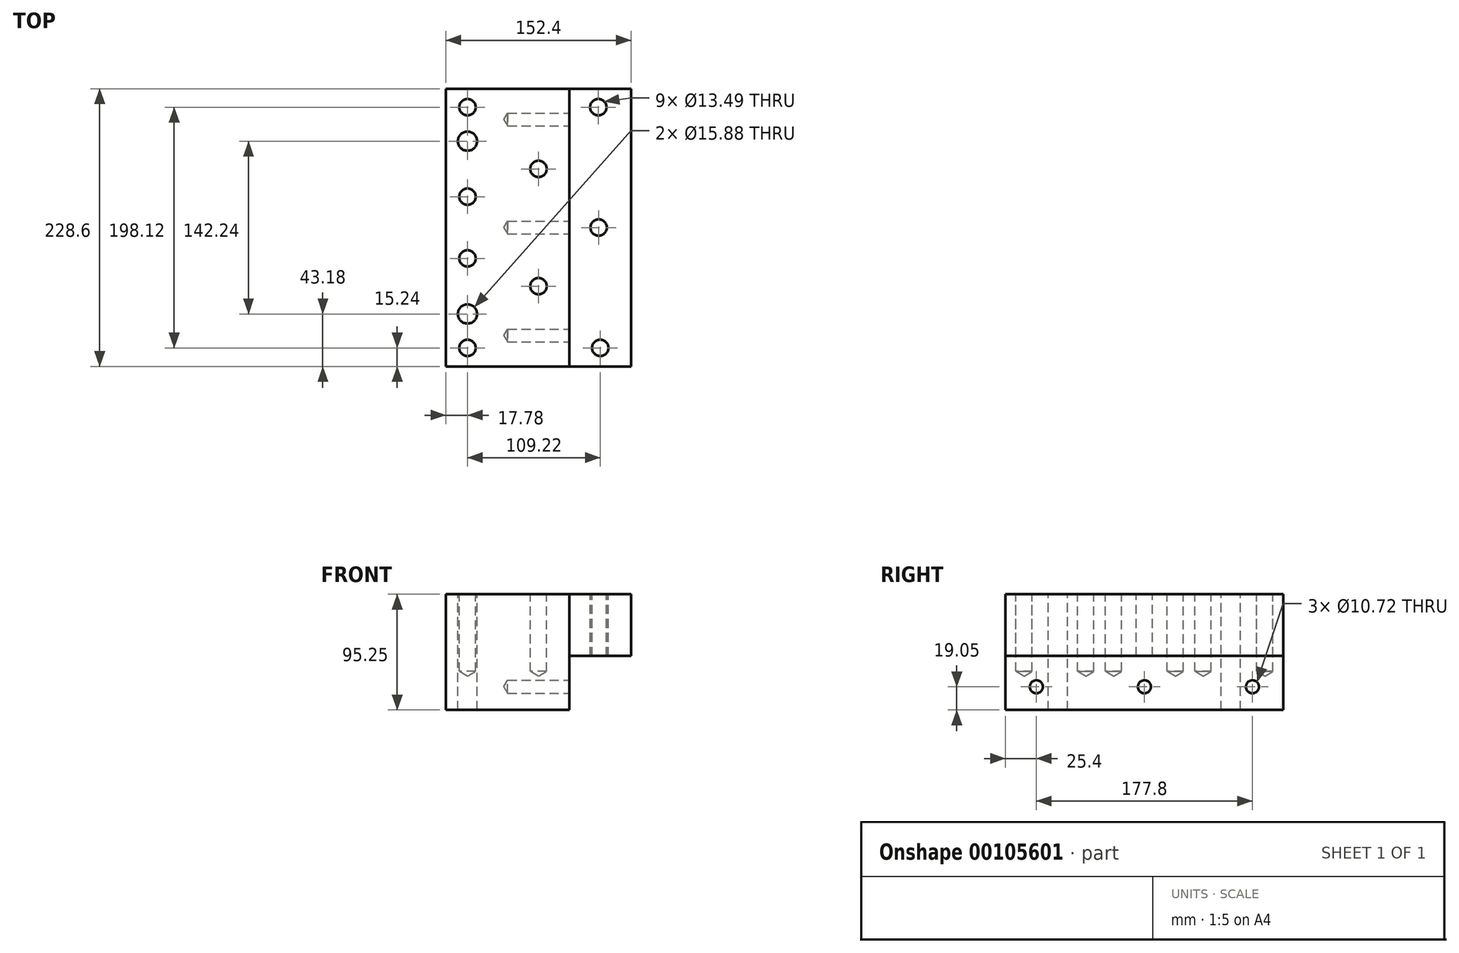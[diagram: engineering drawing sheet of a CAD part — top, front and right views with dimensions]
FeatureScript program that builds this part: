
annotation { "Feature Type Name" : "Feature", "Feature Type Description" : "" }
export const myFeature = defineFeature(function(context is Context, id is Id, definition is map)
    precondition{}
    {
        {
            var Q0;
            Q0=qCreatedBy(makeId("Top.planeOp"),FACE);
            var sketch = newSketch(context, id + "F0", { "sketchPlane" : qUnion([Q0])});
            skLineSegment(sketch, "E0.bottom", {"start": v(-76.2, 114.3) * mm, "end": v(76.2, 114.3) * mm});
            skLineSegment(sketch, "E0.top", {"start": v(-76.2, -114.3) * mm, "end": v(76.2, -114.3) * mm});
            skLineSegment(sketch, "E0.left", {"start": v(-76.2, 114.3) * mm, "end": v(-76.2, -114.3) * mm});
            skLineSegment(sketch, "E0.right", {"start": v(76.2, 114.3) * mm, "end": v(76.2, -114.3) * mm});
            skPoint(sketch, "E0.middle", {"position": v(0, 0) * mm});
            skLineSegment(sketch, "E1", {"start": v(25.4, 114.3) * mm, "end": v(25.4, -114.3) * mm});
            skSolve(sketch);
        }
        {
            var Q0;
            {var subQ0=sQuery(id+"F0.wireOp",EDGE,"E0.left");Q0=makeQuery(id+"F0.imprint","IMPRINT",FACE,{"disambiguationData":[TD([[makeQuery(id+"F0.imprint","IMPRINT",EDGE,{"derivedFrom":subQ0}),1.0]])]});}
            extrude(context, id + "F1", {"entities" : qUnion([Q0]), "oppositeDirection" : true, "depth" : 95.25 * mm});
        }
        {
            var Q0;
            {var subQ0=sQuery(id+"F0.wireOp",EDGE,"E0.right");Q0=makeQuery(id+"F0.imprint","IMPRINT",FACE,{"disambiguationData":[TD([[makeQuery(id+"F0.imprint","IMPRINT",EDGE,{"derivedFrom":subQ0}),-1.0]])]});}
            extrude(context, id + "F2", {"entities" : qUnion([Q0]), "oppositeDirection" : true, "depth" : 50.8 * mm});
        }
        {
            var Q0;
            Q0=makeQuery(id+"F1.opExtrude","CAP_FACE",FACE,{"disambiguationData":[OSD([sQuery(id+"F0.wireOp",EDGE,"E0.bottom"),sQuery(id+"F0.wireOp",EDGE,"E0.top"),sQuery(id+"F0.wireOp",EDGE,"E0.left"),sQuery(id+"F0.wireOp",EDGE,"E1")])],"isStart":true});
            var sketch = newSketch(context, id + "F3", { "sketchPlane" : qUnion([Q0])});
            skPoint(sketch, "E2", {"position": v(-58.42, -99.06) * mm});
            skPoint(sketch, "E3", {"position": v(-58.42, -25.4) * mm});
            skPoint(sketch, "E4", {"position": v(-58.42, 25.4) * mm});
            skPoint(sketch, "E5", {"position": v(-58.42, 99.06) * mm});
            skPoint(sketch, "E6", {"position": v(-58.42, 71.12) * mm});
            skPoint(sketch, "E7", {"position": v(-58.42, -71.12) * mm});
            skPoint(sketch, "E8", {"position": v(0, -48.26) * mm});
            skPoint(sketch, "E9", {"position": v(0, 48.26) * mm});
            skPoint(sketch, "E10", {"position": v(50.8, -99.06) * mm});
            skPoint(sketch, "E11", {"position": v(49.5, 0) * mm});
            skPoint(sketch, "E12", {"position": v(49.22, 99.06) * mm});
            skSolve(sketch);
        }
        {
            var Q0;
            Q0=sQuery(id+"F3.wireOp",VERTEX,"E5");
            var Q1;
            Q1=sQuery(id+"F3.wireOp",VERTEX,"E4");
            var Q2;
            Q2=sQuery(id+"F3.wireOp",VERTEX,"E3");
            var Q3;
            Q3=sQuery(id+"F3.wireOp",VERTEX,"E2");
            var Q4;
            Q4=sQuery(id+"F3.wireOp",VERTEX,"E10");
            var Q5;
            Q5=sQuery(id+"F3.wireOp",VERTEX,"E11");
            var Q6;
            Q6=sQuery(id+"F3.wireOp",VERTEX,"E12");
            var Q7;
            Q7=sQuery(id+"F3.wireOp",VERTEX,"E9");
            var Q8;
            Q8=sQuery(id+"F3.wireOp",VERTEX,"E8");
            var Q9;
            Q9=makeQuery(id+"F1.opExtrude","SWEPT_BODY",BODY,{"disambiguationData":[OSD([sQuery(id+"F0.wireOp",EDGE,"E0.bottom"),sQuery(id+"F0.wireOp",EDGE,"E0.top"),sQuery(id+"F0.wireOp",EDGE,"E0.left"),sQuery(id+"F0.wireOp",EDGE,"E1")])]});
            hole(context, id + "F4", {"style" : HoleStyle.SIMPLE, "endStyle" : HoleEndStyle.BLIND, "holeDiameter" : 13.5 * mm, "holeDepth" : 63.5 * mm, "locations" : qUnion([Q0, Q1, Q2, Q3, Q4, Q5, Q6, Q7, Q8]), "scope" : qUnion([Q9])});
        }
        {
            var Q0;
            Q0=sQuery(id+"F3.wireOp",VERTEX,"E12");
            var Q1;
            Q1=sQuery(id+"F3.wireOp",VERTEX,"E11");
            var Q2;
            Q2=sQuery(id+"F3.wireOp",VERTEX,"E10");
            var Q3;
            Q3=makeQuery(id+"F2.opExtrude","SWEPT_BODY",BODY,{"disambiguationData":[OSD([sQuery(id+"F0.wireOp",EDGE,"E0.bottom"),sQuery(id+"F0.wireOp",EDGE,"E0.top"),sQuery(id+"F0.wireOp",EDGE,"E0.right"),sQuery(id+"F0.wireOp",EDGE,"E1")])]});
            hole(context, id + "F5", {"style" : HoleStyle.SIMPLE, "endStyle" : HoleEndStyle.BLIND, "holeDiameter" : 13.5 * mm, "holeDepth" : 63.5 * mm, "locations" : qUnion([Q0, Q1, Q2]), "scope" : qUnion([Q3])});
        }
        {
            var Q0;
            Q0=sQuery(id+"F3.wireOp",VERTEX,"E6");
            var Q1;
            Q1=sQuery(id+"F3.wireOp",VERTEX,"E7");
            var Q2;
            Q2=makeQuery(id+"F1.opExtrude","SWEPT_BODY",BODY,{"disambiguationData":[OSD([sQuery(id+"F0.wireOp",EDGE,"E0.bottom"),sQuery(id+"F0.wireOp",EDGE,"E0.top"),sQuery(id+"F0.wireOp",EDGE,"E0.left"),sQuery(id+"F0.wireOp",EDGE,"E1")])]});
            hole(context, id + "F6", {"style" : HoleStyle.SIMPLE, "endStyle" : HoleEndStyle.THROUGH, "holeDiameter" : 15.88 * mm, "locations" : qUnion([Q0, Q1]), "scope" : qUnion([Q2]), "isTappedThrough" : true});
        }
        {
            var Q0;
            Q0=makeQuery(id+"F1.opExtrude","SWEPT_FACE",FACE,{"disambiguationData":[OSD([sQuery(id+"F0.wireOp",EDGE,"E1")])]});
            var sketch = newSketch(context, id + "F7", { "sketchPlane" : qUnion([Q0])});
            skPoint(sketch, "E13", {"position": v(-88.9, -76.2) * mm});
            skPoint(sketch, "E14", {"position": v(0, -76.2) * mm});
            skPoint(sketch, "E15", {"position": v(88.9, -76.2) * mm});
            skSolve(sketch);
        }
        {
            var Q0;
            Q0=sQuery(id+"F7.wireOp",VERTEX,"E13");
            var Q1;
            Q1=sQuery(id+"F7.wireOp",VERTEX,"E14");
            var Q2;
            Q2=sQuery(id+"F7.wireOp",VERTEX,"E15");
            var Q3;
            Q3=makeQuery(id+"F1.opExtrude","SWEPT_BODY",BODY,{"disambiguationData":[OSD([sQuery(id+"F0.wireOp",EDGE,"E0.bottom"),sQuery(id+"F0.wireOp",EDGE,"E0.top"),sQuery(id+"F0.wireOp",EDGE,"E0.left"),sQuery(id+"F0.wireOp",EDGE,"E1")])]});
            hole(context, id + "F8", {"style" : HoleStyle.SIMPLE, "endStyle" : HoleEndStyle.BLIND, "holeDiameter" : 10.72 * mm, "holeDepth" : 50.8 * mm, "locations" : qUnion([Q0, Q1, Q2]), "scope" : qUnion([Q3])});
        }
    });
